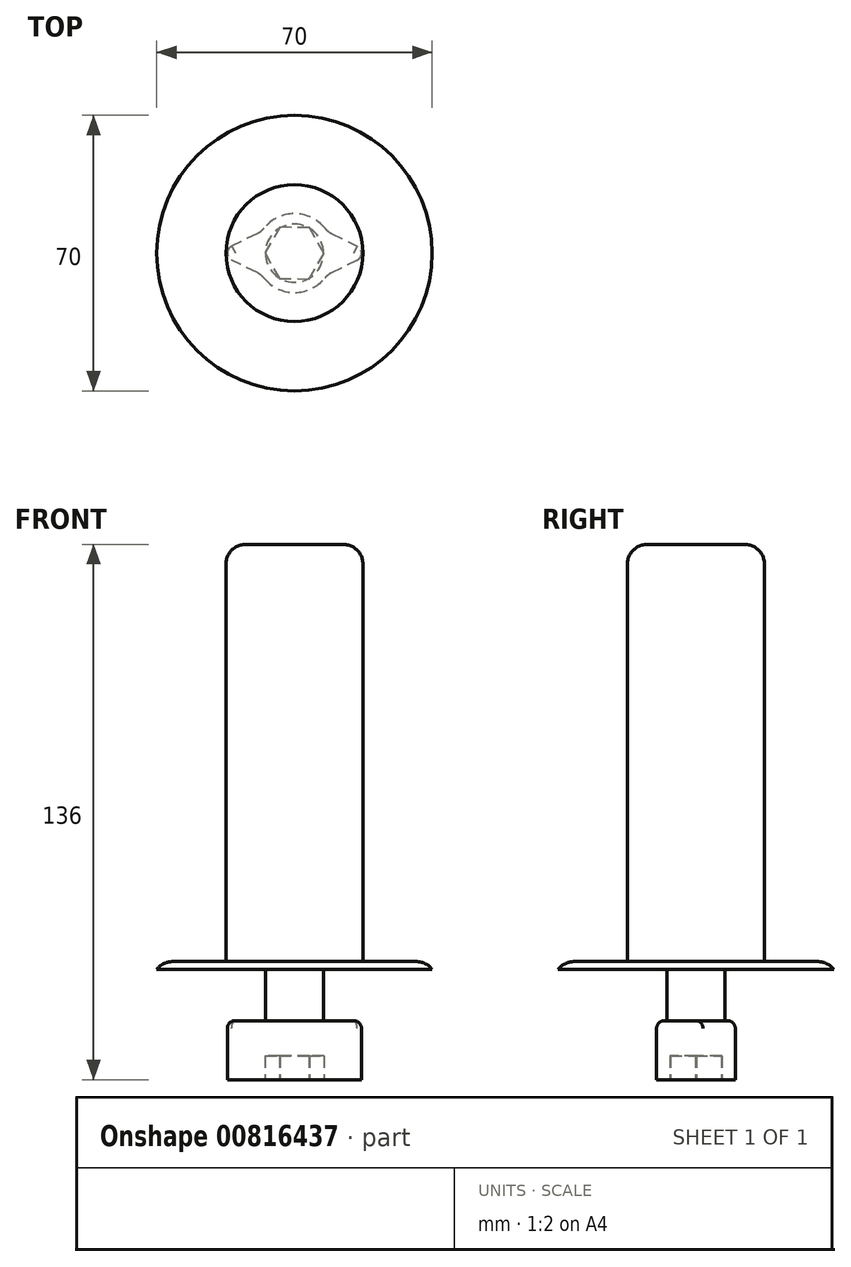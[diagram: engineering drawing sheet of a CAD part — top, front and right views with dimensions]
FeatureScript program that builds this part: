
annotation { "Feature Type Name" : "Feature", "Feature Type Description" : "" }
export const myFeature = defineFeature(function(context is Context, id is Id, definition is map)
    precondition{}
    {
        {
            var Q0;
            Q0=qCreatedBy(makeId("Top.planeOp"),FACE);
            var sketch = newSketch(context, id + "F0", { "sketchPlane" : qUnion([Q0])});
            skArc(sketch, "E0", {"start": v(-8.34, -5.52) * mm, "mid": v(0, -10) * mm, "end": v(8.34, -5.52) * mm});
            skLineSegment(sketch, "E1", {"start": v(0, 0) * mm, "end": v(0, -44.2) * mm, "construction": true});
            skLineSegment(sketch, "E2", {"start": v(0, 0) * mm, "end": v(61.46, 0) * mm, "construction": true});
            skLineSegment(sketch, "E3", {"start": v(8.34, 5.52) * mm, "end": v(18, 0.77) * mm});
            skLineSegment(sketch, "E4.MirrorCS", {"start": v(8.34, -5.52) * mm, "end": v(18, -0.77) * mm});
            skLineSegment(sketch, "E5", {"start": v(18, 0.77) * mm, "end": v(18, -0.77) * mm});
            skLineSegment(sketch, "E6.MirrorCS", {"start": v(-8.34, 5.52) * mm, "end": v(-18, 0.77) * mm});
            skLineSegment(sketch, "E7.MirrorCS", {"start": v(-8.34, -5.52) * mm, "end": v(-18, -0.77) * mm});
            skLineSegment(sketch, "E8.MirrorCS", {"start": v(-18, 0.77) * mm, "end": v(-18, -0.77) * mm});
            skArc(sketch, "E9.trimOffspring", {"start": v(8.34, 5.52) * mm, "mid": v(0, 10) * mm, "end": v(-8.34, 5.52) * mm});
            skSolve(sketch);
        }
        {
            var Q0;
            Q0=makeQuery(id+"F0.imprint","IMPRINT",FACE,{"disambiguationData":[TD([[makeQuery(id+"F0.imprint","IMPRINT",EDGE,{"derivedFrom":sQuery(id+"F0.wireOp",EDGE,"E0")}),1.0]])]});
            extrude(context, id + "F1", {"entities" : qUnion([Q0]), "depth" : 15 * mm, "offsetDistance" : 25 * mm});
        }
        {
            var Q0;
            Q0=makeQuery(id+"F1.opExtrude","CAP_FACE",FACE,{"disambiguationData":[OSD([sQuery(id+"F0.wireOp",EDGE,"E0"),sQuery(id+"F0.wireOp",EDGE,"E3"),sQuery(id+"F0.wireOp",EDGE,"E4.MirrorCS"),sQuery(id+"F0.wireOp",EDGE,"E5"),sQuery(id+"F0.wireOp",EDGE,"E6.MirrorCS"),sQuery(id+"F0.wireOp",EDGE,"E7.MirrorCS"),sQuery(id+"F0.wireOp",EDGE,"E8.MirrorCS"),sQuery(id+"F0.wireOp",EDGE,"E9.trimOffspring")])],"isStart":true});
            var sketch = newSketch(context, id + "F2", { "sketchPlane" : qUnion([Q0])});
            skCircle(sketch, "E10.cCircle", {"center": v(0, 0) * mm, "radius": 6.5 * mm, "construction": true});
            skLineSegment(sketch, "E10.0", {"start": v(-7.5, -0.1) * mm, "end": v(-3.84, 6.45) * mm});
            skLineSegment(sketch, "E10.1", {"start": v(-3.84, 6.45) * mm, "end": v(3.66, 6.55) * mm});
            skLineSegment(sketch, "E10.2", {"start": v(3.66, 6.55) * mm, "end": v(7.5, 0.1) * mm});
            skLineSegment(sketch, "E10.3", {"start": v(7.5, 0.1) * mm, "end": v(3.84, -6.45) * mm});
            skLineSegment(sketch, "E10.4", {"start": v(3.84, -6.45) * mm, "end": v(-3.66, -6.55) * mm});
            skLineSegment(sketch, "E10.5", {"start": v(-3.66, -6.55) * mm, "end": v(-7.5, -0.1) * mm});
            skPoint(sketch, "E10.0.midPoint", {"position": v(-5.67, 3.17) * mm});
            skSolve(sketch);
        }
        {
            var Q0;
            Q0=makeQuery(id+"F2.imprint","IMPRINT",FACE,{"disambiguationData":[TD([[makeQuery(id+"F2.imprint","IMPRINT",EDGE,{"derivedFrom":sQuery(id+"F2.wireOp",EDGE,"E10.0")}),-1.0]])]});
            extrude(context, id + "F3", {"entities" : qUnion([Q0]), "operationType" : NewBodyOperationType.REMOVE, "oppositeDirection" : true, "depth" : 6 * mm, "offsetDistance" : 25 * mm});
        }
        {
            var Q0;
            Q0=makeQuery(id+"F1.opExtrude","SWEPT_EDGE",EDGE,{"disambiguationData":[OSD([sQuery(id+"F0.wireOp",EDGE,"E7.MirrorCS"),sQuery(id+"F0.wireOp",EDGE,"E8.MirrorCS")])]});
            var Q1;
            Q1=makeQuery(id+"F1.opExtrude","SWEPT_EDGE",EDGE,{"disambiguationData":[OSD([sQuery(id+"F0.wireOp",EDGE,"E6.MirrorCS"),sQuery(id+"F0.wireOp",EDGE,"E8.MirrorCS")])]});
            var Q2;
            Q2=makeQuery(id+"F1.opExtrude","SWEPT_EDGE",EDGE,{"disambiguationData":[OSD([sQuery(id+"F0.wireOp",EDGE,"E4.MirrorCS"),sQuery(id+"F0.wireOp",EDGE,"E5")])]});
            var Q3;
            Q3=makeQuery(id+"F1.opExtrude","SWEPT_EDGE",EDGE,{"disambiguationData":[OSD([sQuery(id+"F0.wireOp",EDGE,"E3"),sQuery(id+"F0.wireOp",EDGE,"E5")])]});
            fillet(context, id + "F4", {"entities" : qUnion([Q0, Q1, Q2, Q3]), "radius" : 2 * mm, "tangentPropagation" : true, "allowEdgeOverflow" : false});
        }
        {
            var Q0;
            Q0=makeQuery(id+"F1.opExtrude","SWEPT_EDGE",EDGE,{"disambiguationData":[OSD([sQuery(id+"F0.wireOp",EDGE,"E6.MirrorCS"),sQuery(id+"F0.wireOp",EDGE,"E9.trimOffspring")])]});
            var Q1;
            Q1=makeQuery(id+"F1.opExtrude","SWEPT_EDGE",EDGE,{"disambiguationData":[OSD([sQuery(id+"F0.wireOp",EDGE,"E3"),sQuery(id+"F0.wireOp",EDGE,"E9.trimOffspring")])]});
            var Q2;
            Q2=makeQuery(id+"F1.opExtrude","SWEPT_EDGE",EDGE,{"disambiguationData":[OSD([sQuery(id+"F0.wireOp",EDGE,"E0"),sQuery(id+"F0.wireOp",EDGE,"E4.MirrorCS")])]});
            var Q3;
            Q3=makeQuery(id+"F1.opExtrude","SWEPT_EDGE",EDGE,{"disambiguationData":[OSD([sQuery(id+"F0.wireOp",EDGE,"E0"),sQuery(id+"F0.wireOp",EDGE,"E7.MirrorCS")])]});
            fillet(context, id + "F5", {"entities" : qUnion([Q0, Q1, Q2, Q3]), "radius" : 5 * mm, "tangentPropagation" : true, "allowEdgeOverflow" : false});
        }
        {
            var Q0;
            {var subQ0=sQuery(id+"F0.wireOp",EDGE,"E9.trimOffspring");var subQ1=sQuery(id+"F0.wireOp",EDGE,"E6.MirrorCS");Q0=makeQuery(id+"F5.opFillet","BLEND_EDGE",EDGE,{"blendedFrom":[makeQuery(id+"F1.opExtrude","SWEPT_EDGE",EDGE,{"disambiguationData":[OSD([subQ1,subQ0])]}),makeQuery(id+"F1.opExtrude","CAP_FACE",FACE,{"disambiguationData":[OSD([sQuery(id+"F0.wireOp",EDGE,"E0"),sQuery(id+"F0.wireOp",EDGE,"E3"),sQuery(id+"F0.wireOp",EDGE,"E4.MirrorCS"),sQuery(id+"F0.wireOp",EDGE,"E5"),subQ1,sQuery(id+"F0.wireOp",EDGE,"E7.MirrorCS"),sQuery(id+"F0.wireOp",EDGE,"E8.MirrorCS"),subQ0])],"isStart":false})],"blendedInto":[makeQuery(id+"F1.opExtrude","CAP_FACE",FACE,{"disambiguationData":[OSD([sQuery(id+"F0.wireOp",EDGE,"E0"),sQuery(id+"F0.wireOp",EDGE,"E3"),sQuery(id+"F0.wireOp",EDGE,"E4.MirrorCS"),sQuery(id+"F0.wireOp",EDGE,"E5"),subQ1,sQuery(id+"F0.wireOp",EDGE,"E7.MirrorCS"),sQuery(id+"F0.wireOp",EDGE,"E8.MirrorCS"),subQ0])],"isStart":false})]});}
            fillet(context, id + "F6", {"entities" : qUnion([Q0]), "radius" : 2 * mm, "tangentPropagation" : true, "allowEdgeOverflow" : false});
        }
        {
            var Q0;
            Q0=makeQuery(id+"F1.opExtrude","CAP_EDGE",EDGE,{"disambiguationData":[OSD([sQuery(id+"F0.wireOp",EDGE,"E7.MirrorCS")])],"isStart":false});
            fillet(context, id + "F7", {"entities" : qUnion([Q0]), "radius" : 2 * mm, "tangentPropagation" : true, "allowEdgeOverflow" : false});
        }
        {
            var Q0;
            Q0=makeQuery(id+"F1.opExtrude","CAP_FACE",FACE,{"disambiguationData":[OSD([sQuery(id+"F0.wireOp",EDGE,"E0"),sQuery(id+"F0.wireOp",EDGE,"E3"),sQuery(id+"F0.wireOp",EDGE,"E4.MirrorCS"),sQuery(id+"F0.wireOp",EDGE,"E5"),sQuery(id+"F0.wireOp",EDGE,"E6.MirrorCS"),sQuery(id+"F0.wireOp",EDGE,"E7.MirrorCS"),sQuery(id+"F0.wireOp",EDGE,"E8.MirrorCS"),sQuery(id+"F0.wireOp",EDGE,"E9.trimOffspring")])],"isStart":false});
            var sketch = newSketch(context, id + "F8", { "sketchPlane" : qUnion([Q0])});
            skSolve(sketch);
        }
        {
            var Q0;
            {var subQ0=sQuery(id+"F0.wireOp",EDGE,"E9.trimOffspring");var subQ1=sQuery(id+"F0.wireOp",EDGE,"E7.MirrorCS");var subQ2=sQuery(id+"F0.wireOp",EDGE,"E6.MirrorCS");var subQ3=sQuery(id+"F0.wireOp",EDGE,"E4.MirrorCS");var subQ4=sQuery(id+"F0.wireOp",EDGE,"E3");var subQ5=sQuery(id+"F0.wireOp",EDGE,"E0");var subQ6=makeQuery(id+"F1.opExtrude","CAP_FACE",FACE,{"disambiguationData":[OSD([subQ5,subQ4,subQ3,sQuery(id+"F0.wireOp",EDGE,"E5"),subQ2,subQ1,sQuery(id+"F0.wireOp",EDGE,"E8.MirrorCS"),subQ0])],"isStart":false});var subQ7=subQ6;Q0=makeQuery(id+"F8.imprint","IMPRINT",FACE,{"disambiguationData":[TD([[makeQuery(id+"F8.imprint","IMPRINT",EDGE,{"derivedFrom":makeQuery(id+"F6.opFillet","BLEND_EDGE",EDGE,{"blendedFrom":[makeQuery(id+"F1.opExtrude","CAP_EDGE",EDGE,{"disambiguationData":[OSD([subQ0])],"isStart":false}),subQ7],"blendedInto":[subQ7]})}),1.0]])]});}
            var sketch = newSketch(context, id + "F9", { "sketchPlane" : qUnion([Q0])});
            skCircle(sketch, "E11", {"center": v(0, 0) * mm, "radius": 7.37 * mm});
            skSolve(sketch);
        }
        {
            var Q0;
            Q0=makeQuery(id+"F9.imprint","IMPRINT",FACE,{"disambiguationData":[TD([[makeQuery(id+"F9.imprint","IMPRINT",EDGE,{"derivedFrom":sQuery(id+"F9.wireOp",EDGE,"E11")}),1.0]])]});
            var sketch = newSketch(context, id + "F10", { "sketchPlane" : qUnion([Q0])});
            skSolve(sketch);
        }
        {
            var Q0;
            Q0=makeQuery(id+"F10.imprint","IMPRINT",FACE,{"disambiguationData":[TD([[makeQuery(id+"F10.imprint","IMPRINT",EDGE,{"derivedFrom":makeQuery(id+"F9.imprint","IMPRINT",EDGE,{"derivedFrom":sQuery(id+"F9.wireOp",EDGE,"E11")})}),1.0]])]});
            extrude(context, id + "F11", {"entities" : qUnion([Q0]), "operationType" : NewBodyOperationType.ADD, "depth" : 120 * mm, "offsetDistance" : 25 * mm});
        }
        {
            var Q0;
            Q0=makeQuery(id+"F11.opExtrude","CAP_EDGE",EDGE,{"disambiguationData":[OSD([sQuery(id+"F9.wireOp",EDGE,"E11")])],"isStart":false});
            fillet(context, id + "F12", {"entities" : qUnion([Q0]), "radius" : 5 * mm, "tangentPropagation" : true, "allowEdgeOverflow" : false});
        }
        {
            var Q0;
            Q0=qCreatedBy(makeId("Top.planeOp"),FACE);
            var sketch = newSketch(context, id + "F13", { "sketchPlane" : qUnion([Q0])});
            skCircle(sketch, "E12", {"center": v(0, 0) * mm, "radius": 17.4 * mm});
            skSolve(sketch);
        }
        {
            var Q0;
            Q0 = qSketchRegion(id + "F13", true);
            extrude(context, id + "F14", {"entities" : qUnion([Q0]), "operationType" : NewBodyOperationType.ADD, "depth" : 136 * mm, "offsetDistance" : 25 * mm, "hasSecondDirection" : true, "secondDirectionOppositeDirection" : false, "secondDirectionDepth" : 28 * mm});
        }
        {
            var Q0;
            Q0=makeQuery(id+"F14.opExtrude","CAP_EDGE",EDGE,{"disambiguationData":[OSD([sQuery(id+"F13.wireOp",EDGE,"E12")])],"isStart":false});
            fillet(context, id + "F15", {"entities" : qUnion([Q0]), "radius" : 5 * mm, "tangentPropagation" : true, "allowEdgeOverflow" : false});
        }
        {
            var Q0;
            Q0=qCreatedBy(makeId("Top.planeOp"),FACE);
            var sketch = newSketch(context, id + "F16", { "sketchPlane" : qUnion([Q0])});
            skCircle(sketch, "E13", {"center": v(0, 0) * mm, "radius": 35 * mm});
            skSolve(sketch);
        }
        {
            var Q0;
            Q0 = qSketchRegion(id + "F16", true);
            extrude(context, id + "F17", {"entities" : qUnion([Q0]), "operationType" : NewBodyOperationType.ADD, "depth" : 30 * mm, "offsetDistance" : 25 * mm, "hasSecondDirection" : true, "secondDirectionOppositeDirection" : false, "secondDirectionDepth" : 28 * mm});
        }
        {
            var Q0;
            Q0=makeQuery(id+"F17.opExtrude","CAP_EDGE",EDGE,{"disambiguationData":[OSD([sQuery(id+"F16.wireOp",EDGE,"E13")])],"isStart":false});
            fillet(context, id + "F18", {"entities" : qUnion([Q0]), "radius" : 5 * mm, "tangentPropagation" : true, "allowEdgeOverflow" : false});
        }
    });
